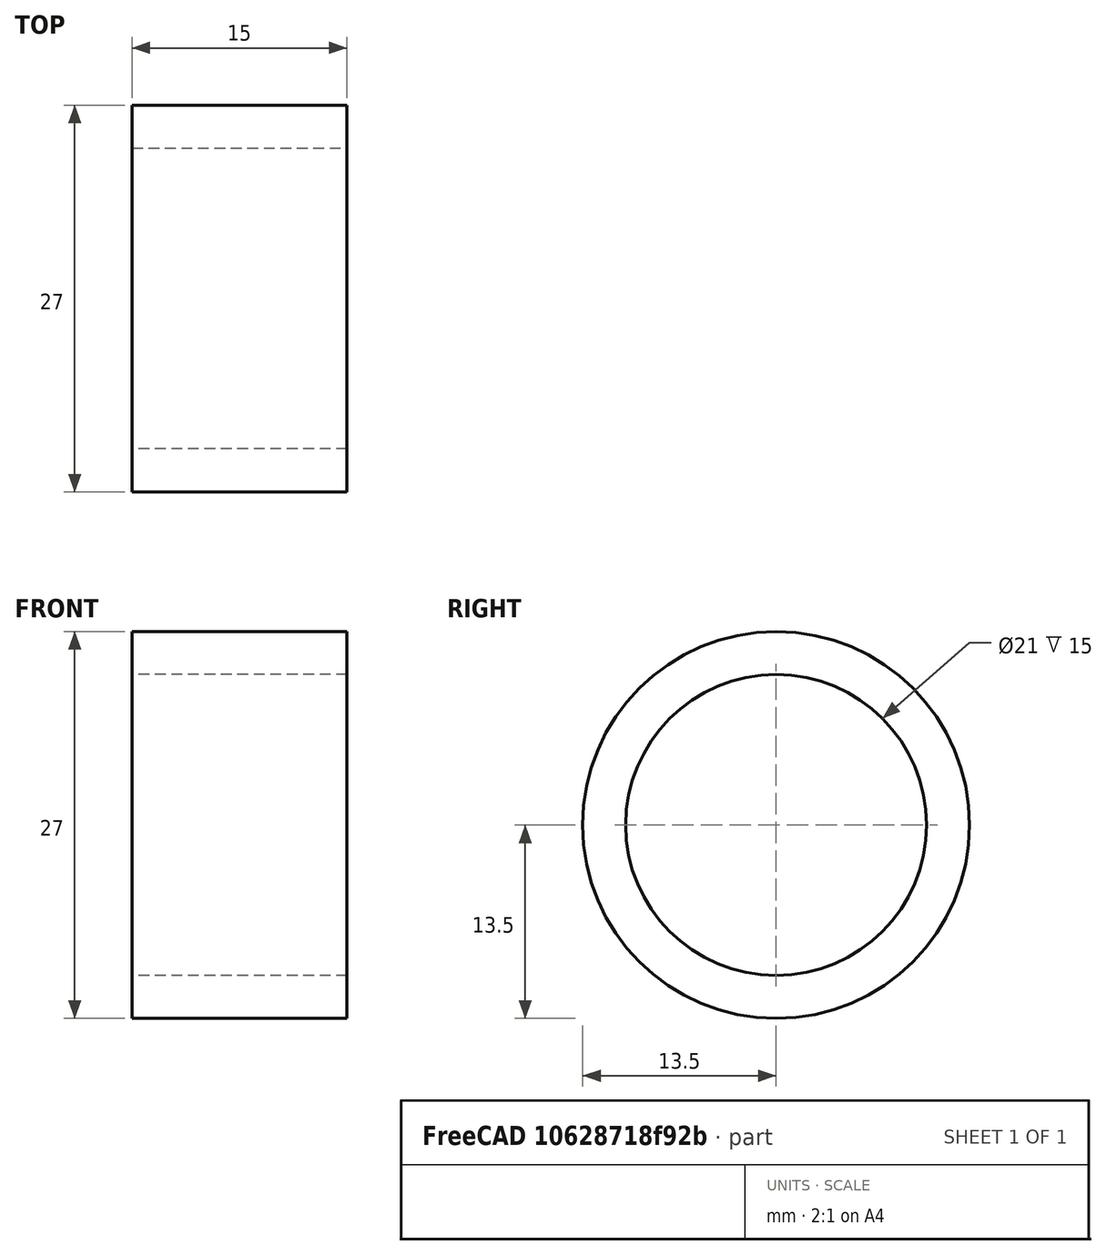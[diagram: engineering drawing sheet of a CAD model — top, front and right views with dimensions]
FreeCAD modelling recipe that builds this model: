
FCSTD DOCUMENT  (FreeCAD 0.18R16131 (Git))
Label: demieTv2_test
License: All rights reserved
LicenseURL: http://en.wikipedia.org/wiki/All_rights_reserved
objects: Sketcher::SketchObject×1, PartDesign::Pad×1, PartDesign::Body×1
note: 4 computed .brp shape members not serialized (recipe doc carries the construction recipe); baked Part::Feature solids carry a one-line shape summary decoded from their .brp

FEATURE [Sketcher::SketchObject] Sketch001
  MapMode = 5
  Placement = pos=(0,0,0) rot=(0.57735,0.57735,0.57735;2.0944rad)
  Support = -> [YZ_Plane]
  sketch-geometry (2):
    g0: Circle CenterX=0 CenterY=14.5 CenterZ=0 NormalX=0 NormalY=0 NormalZ=1 AngleXU=0 Radius=13.5
    g1: Circle CenterX=0 CenterY=14.5 CenterZ=0 NormalX=0 NormalY=0 NormalZ=1 AngleXU=0 Radius=10.5
  constraints (5):
    c: PointOnObject(g0,g-2)
    c: Coincident(g1,g0)
    c: Diameter(g0) = 27
    c: Diameter(g1) = 21
    c: DistanceY(g-1,g0) = 14.5
FEATURE [PartDesign::Pad] Pad001
  Length = 15
  Length2 = 100
  Placement = pos=(0,0,0) rot=(0.57735,0.57735,0.57735;2.0944rad)
  Profile = -> Sketch001
  Type = 0
FEATURE [PartDesign::Body] Body
  Group = -> [Sketch001,Pad001]
  Origin = -> Origin
  Tip = -> Pad001
